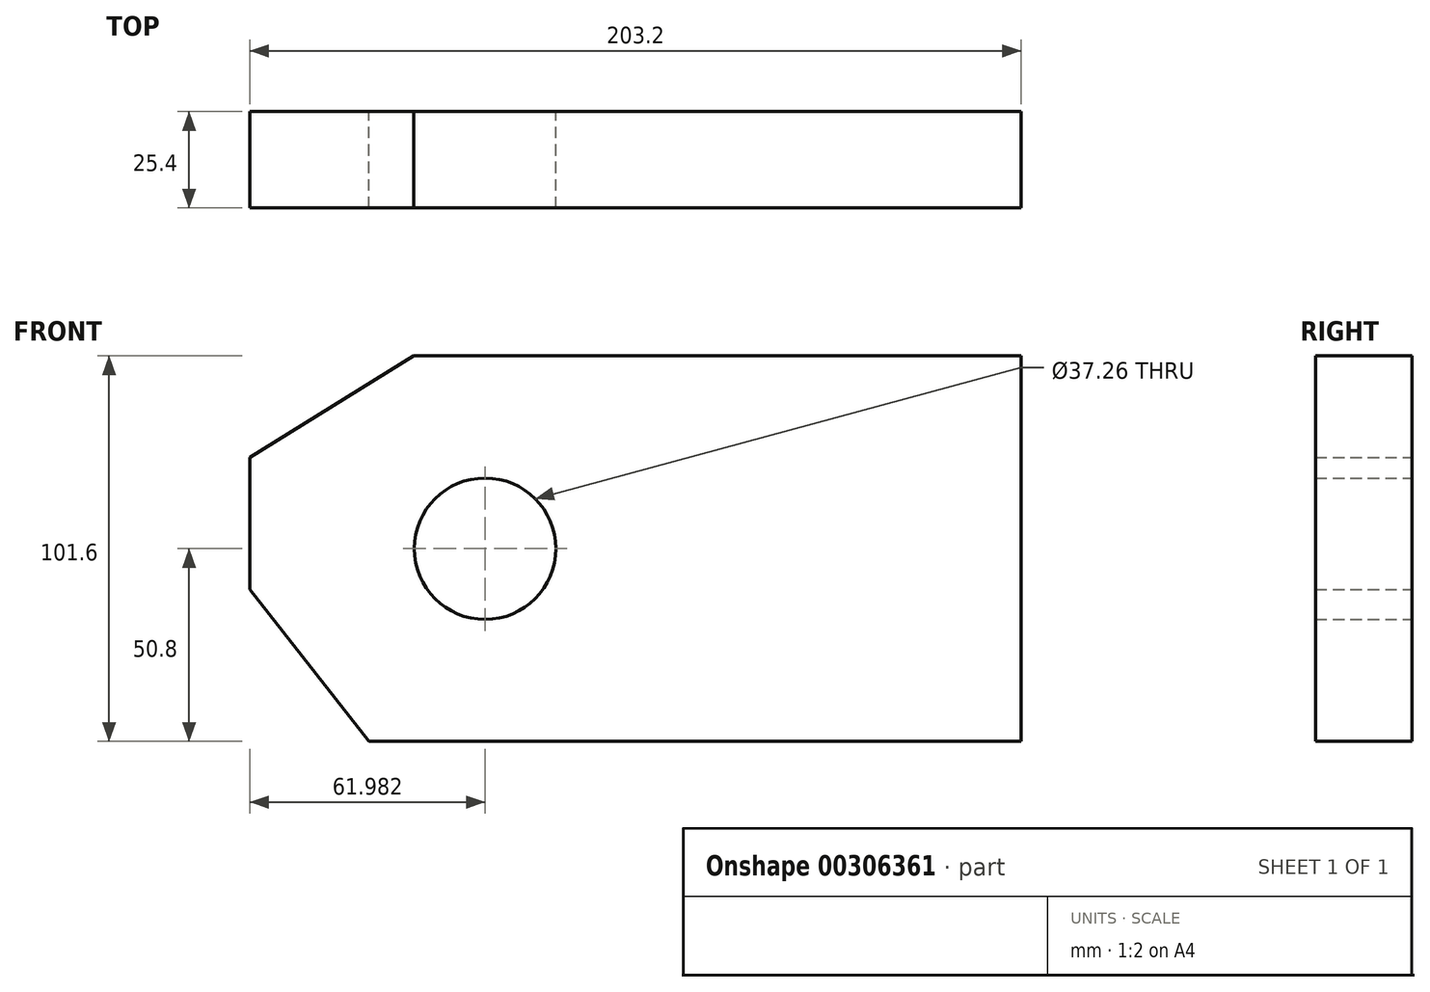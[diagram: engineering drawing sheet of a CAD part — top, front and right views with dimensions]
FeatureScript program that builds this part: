
annotation { "Feature Type Name" : "Feature", "Feature Type Description" : "" }
export const myFeature = defineFeature(function(context is Context, id is Id, definition is map)
    precondition{}
    {
        {
            var Q0;
            Q0=qCreatedBy(makeId("Front.planeOp"),FACE);
            var sketch = newSketch(context, id + "F0", { "sketchPlane" : qUnion([Q0])});
            skLineSegment(sketch, "E0.bottom", {"start": v(-101.6, 50.8) * mm, "end": v(101.6, 50.8) * mm});
            skLineSegment(sketch, "E0.top", {"start": v(-101.6, -50.8) * mm, "end": v(101.6, -50.8) * mm});
            skLineSegment(sketch, "E0.left", {"start": v(-101.6, 50.8) * mm, "end": v(-101.6, -50.8) * mm});
            skLineSegment(sketch, "E0.right", {"start": v(101.6, 50.8) * mm, "end": v(101.6, -50.8) * mm});
            skPoint(sketch, "E0.middle", {"position": v(0, 0) * mm});
            skLineSegment(sketch, "E1", {"start": v(-58.37, 50.8) * mm, "end": v(-101.6, 24.12) * mm});
            skLineSegment(sketch, "E2", {"start": v(-101.6, -10.8) * mm, "end": v(-70.29, -50.8) * mm});
            skCircle(sketch, "E3", {"center": v(-39.62, 0) * mm, "radius": 18.63 * mm});
            skSolve(sketch);
        }
        {
            var Q0;
            {var subQ0=sQuery(id+"F0.wireOp",EDGE,"E0.right");Q0=makeQuery(id+"F0.imprint","IMPRINT",FACE,{"disambiguationData":[TD([[makeQuery(id+"F0.imprint","IMPRINT",EDGE,{"derivedFrom":subQ0}),-1.0]])]});}
            extrude(context, id + "F1", {"entities" : qUnion([Q0]), "depth" : 25.4 * mm});
        }
    });
